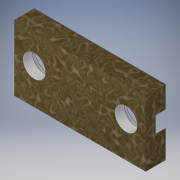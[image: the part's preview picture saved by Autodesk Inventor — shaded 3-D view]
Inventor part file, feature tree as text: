
AUTODESK INVENTOR PART (.ipt)
format: ipt  version: 2017 (Build 210142000, 142)  size: 149,504 bytes
history: native  units: mm
features: extrude x2, sketch x1
ambient origin geometry x8: Origin, YZ Plane, XZ Plane, XY Plane, X Axis, Y Axis, Z Axis, Center Point
bodies: Solid1 (feature_tree)
feature tree (3):
  sketch  "Sketch1"  dims[d2=10.0mm d3=20.0mm d5=6.5mm d8=7.0mm d9=7.0mm d11=3.5mm d12=3.5mm d13=10.0mm d14=3.311677mm d15=4.561677mm d16=1.5mm d17=0.0mm d18=3.0mm d19=0.0mm]
  extrude  "Extrusion1"  Depth=20.0mm
  extrude  "Extrusion2"  Depth=3.0mm
